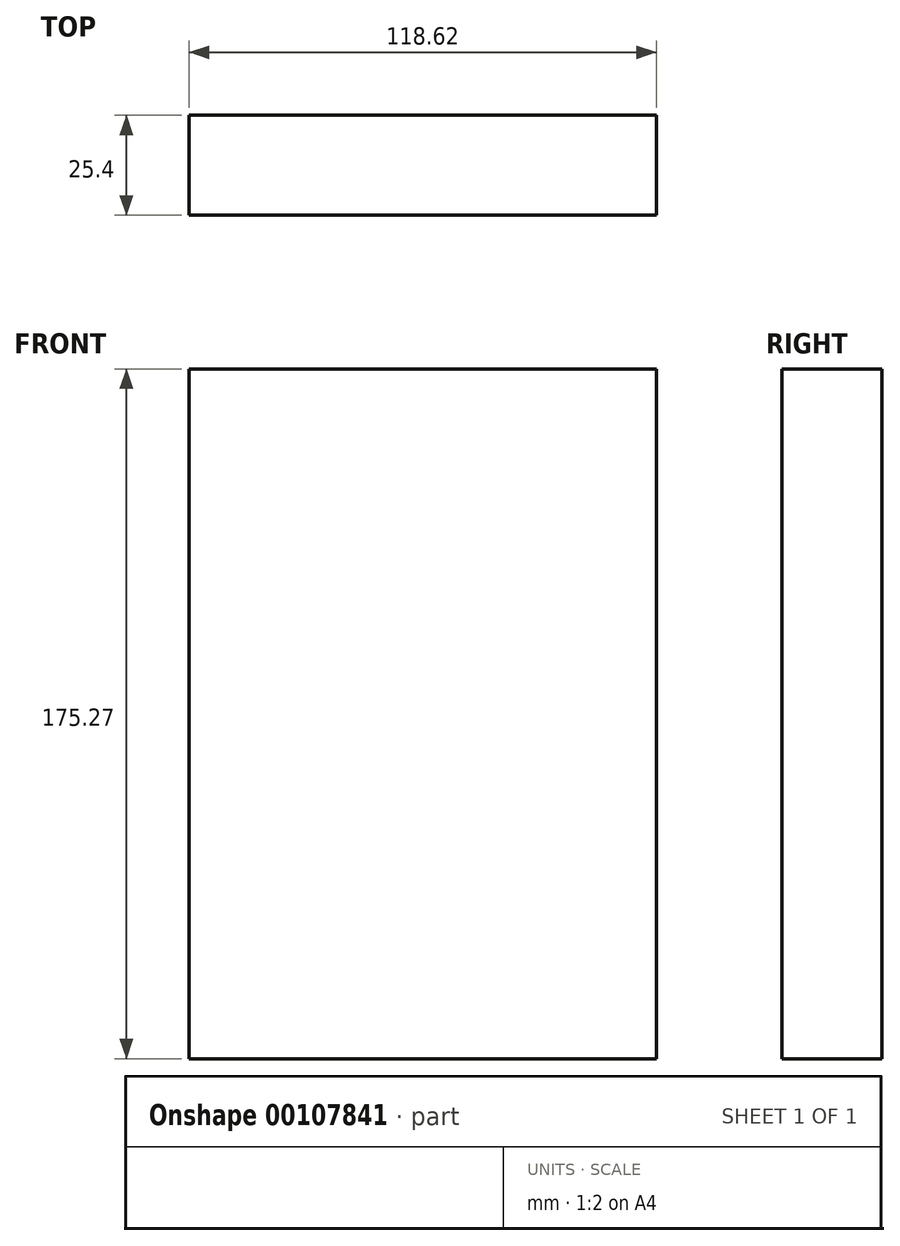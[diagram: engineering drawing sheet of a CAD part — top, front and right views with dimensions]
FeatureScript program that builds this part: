
annotation { "Feature Type Name" : "Feature", "Feature Type Description" : "" }
export const myFeature = defineFeature(function(context is Context, id is Id, definition is map)
    precondition{}
    {
        {
            var Q0;
            Q0=qCreatedBy(makeId("Front.planeOp"),FACE);
            var sketch = newSketch(context, id + "F0", { "sketchPlane" : qUnion([Q0])});
            skLineSegment(sketch, "E0.bottom", {"start": v(-64.43, 101.73) * mm, "end": v(54.2, 101.73) * mm});
            skLineSegment(sketch, "E0.top", {"start": v(-64.43, -73.54) * mm, "end": v(54.2, -73.54) * mm});
            skLineSegment(sketch, "E0.left", {"start": v(-64.43, 101.73) * mm, "end": v(-64.43, -73.54) * mm});
            skLineSegment(sketch, "E0.right", {"start": v(54.2, 101.73) * mm, "end": v(54.2, -73.54) * mm});
            skSolve(sketch);
        }
        {
            var Q0;
            Q0=makeQuery(id+"F0.imprint","IMPRINT",FACE,{"disambiguationData":[TD([[makeQuery(id+"F0.imprint","IMPRINT",EDGE,{"derivedFrom":sQuery(id+"F0.wireOp",EDGE,"E0.bottom")}),-1.0]])]});
            extrude(context, id + "F1", {"entities" : qUnion([Q0]), "depth" : 25.4 * mm});
        }
    });
